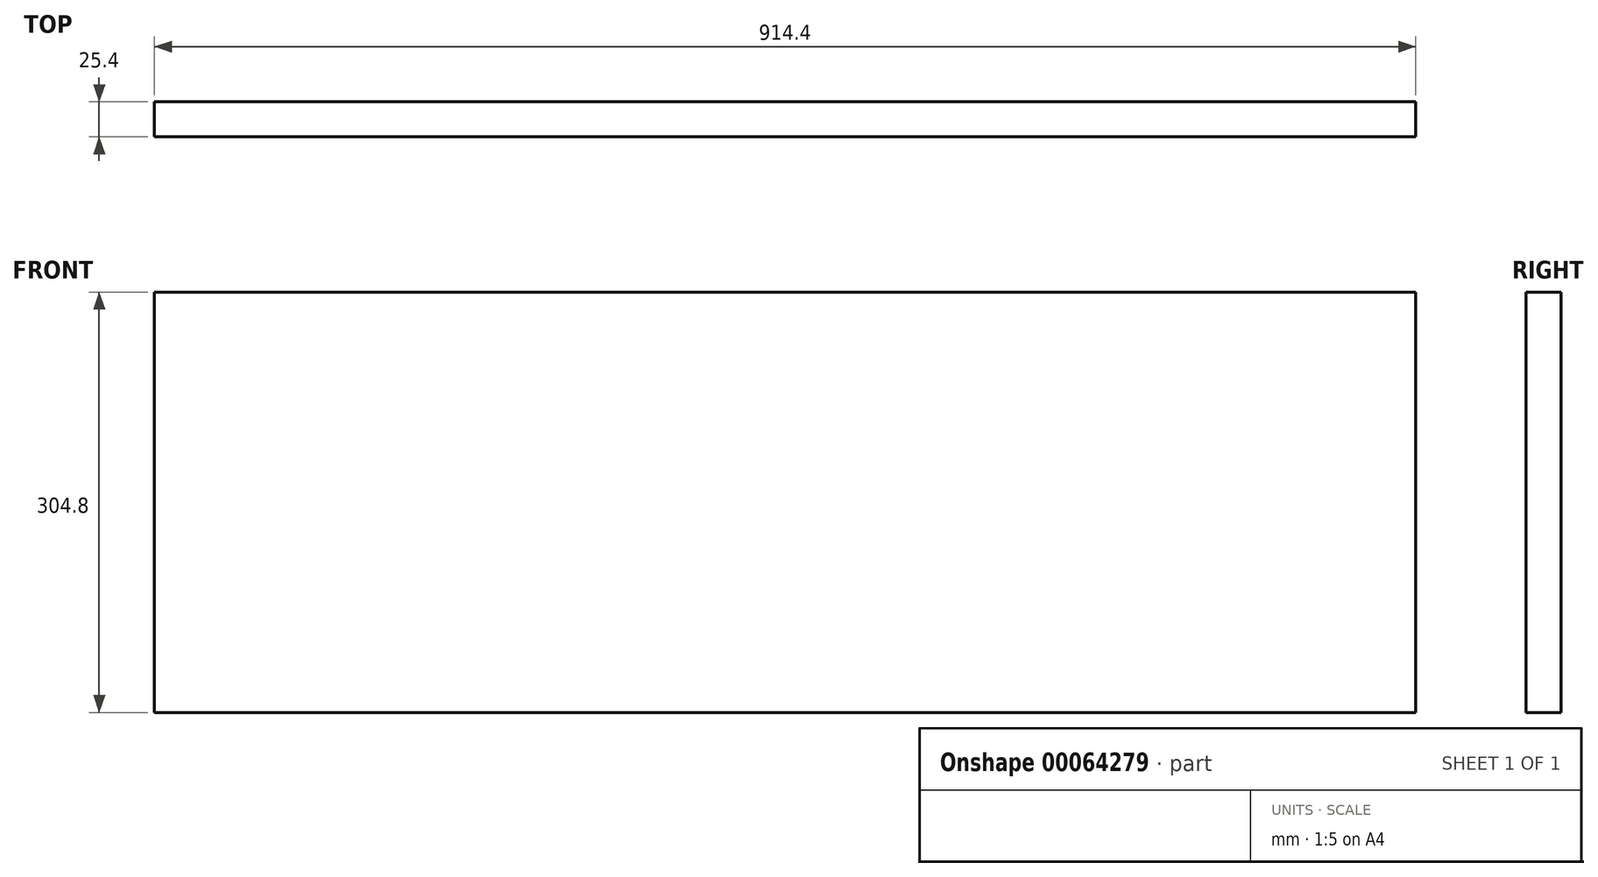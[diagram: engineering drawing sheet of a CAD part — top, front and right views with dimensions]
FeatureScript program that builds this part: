
annotation { "Feature Type Name" : "Feature", "Feature Type Description" : "" }
export const myFeature = defineFeature(function(context is Context, id is Id, definition is map)
    precondition{}
    {
        {
            var Q0;
            Q0=qCreatedBy(makeId("Front.planeOp"),FACE);
            var sketch = newSketch(context, id + "F0", { "sketchPlane" : qUnion([Q0])});
            skLineSegment(sketch, "E0.bottom", {"start": v(-457.2, -152.4) * mm, "end": v(457.2, -152.4) * mm});
            skLineSegment(sketch, "E0.top", {"start": v(-457.2, 152.4) * mm, "end": v(457.2, 152.4) * mm});
            skLineSegment(sketch, "E0.left", {"start": v(-457.2, -152.4) * mm, "end": v(-457.2, 152.4) * mm});
            skLineSegment(sketch, "E0.right", {"start": v(457.2, -152.4) * mm, "end": v(457.2, 152.4) * mm});
            skLineSegment(sketch, "E1", {"start": v(0, 152.4) * mm, "end": v(0, 0) * mm, "construction": true});
            skLineSegment(sketch, "E2", {"start": v(-457.2, 0) * mm, "end": v(0, 0) * mm, "construction": true});
            skSolve(sketch);
        }
        {
            var Q0;
            Q0=makeQuery(id+"F0.imprint","IMPRINT",FACE,{"disambiguationData":[TD([[makeQuery(id+"F0.imprint","IMPRINT",EDGE,{"derivedFrom":sQuery(id+"F0.wireOp",EDGE,"E0.bottom")}),1.0]])]});
            extrude(context, id + "F1", {"entities" : qUnion([Q0]), "depth" : 25.4 * mm});
        }
    });
